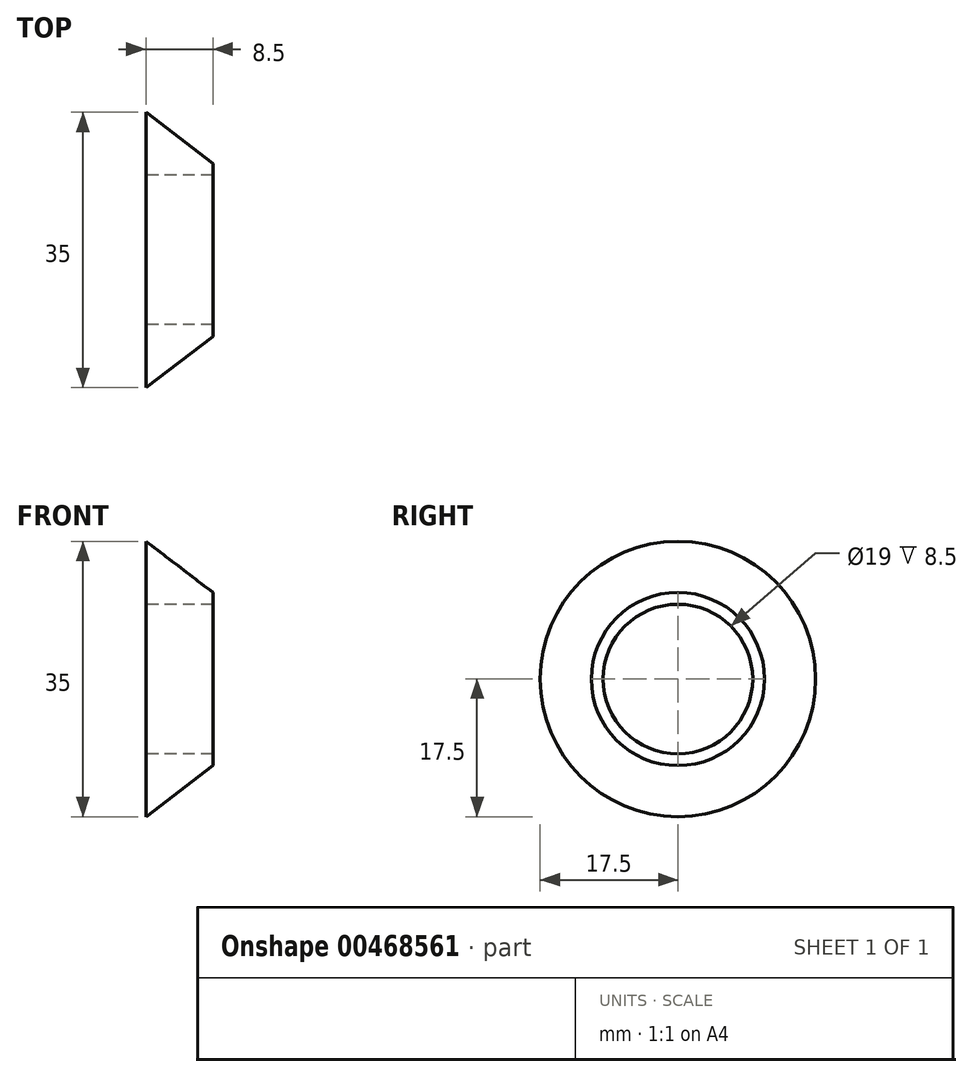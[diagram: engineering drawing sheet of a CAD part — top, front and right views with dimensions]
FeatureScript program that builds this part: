
annotation { "Feature Type Name" : "Feature", "Feature Type Description" : "" }
export const myFeature = defineFeature(function(context is Context, id is Id, definition is map)
    precondition{}
    {
        {
            var Q0;
            Q0=qCreatedBy(makeId("Front.planeOp"),FACE);
            var sketch = newSketch(context, id + "F0", { "sketchPlane" : qUnion([Q0])});
            skLineSegment(sketch, "E0", {"start": v(0, 0) * mm, "end": v(8.5, 0) * mm});
            skLineSegment(sketch, "E1", {"start": v(8.5, 0) * mm, "end": v(8.5, 11) * mm});
            skLineSegment(sketch, "E2", {"start": v(0, 0) * mm, "end": v(0, 17.5) * mm});
            skLineSegment(sketch, "E3", {"start": v(0, 17.5) * mm, "end": v(8.5, 11) * mm});
            skLineSegment(sketch, "E4", {"start": v(0, 9.5) * mm, "end": v(8.5, 9.5) * mm});
            skSolve(sketch);
        }
        {
            var Q0;
            {var subQ0=sQuery(id+"F0.wireOp",EDGE,"E3");Q0=makeQuery(id+"F0.imprint","IMPRINT",FACE,{"disambiguationData":[TD([[makeQuery(id+"F0.imprint","IMPRINT",EDGE,{"derivedFrom":subQ0}),-1.0]])]});}
            var Q1;
            Q1=sQuery(id+"F0.wireOp",EDGE,"E0");
            revolve(context, id + "F1", {"surfaceOperationType" : NewSurfaceOperationType.NEW, "entities" : qUnion([Q0]), "axis" : qUnion([Q1]), "revolveType" : RevolveType.FULL});
        }
    });
